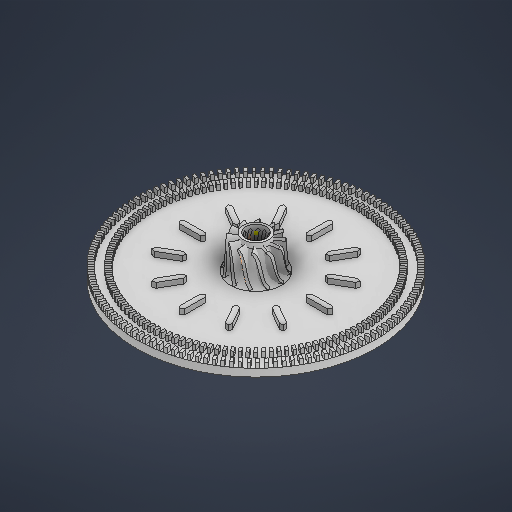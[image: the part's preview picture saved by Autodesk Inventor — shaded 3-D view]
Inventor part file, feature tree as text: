
AUTODESK INVENTOR PART (.ipt)
format: ipt  version: 2025 (Build 290162000, 162)  size: 4,954,624 bytes
history: native  units: mm
features: sketch x10, other x8, extrude x3, pattern_circular x3, revolve x1, projected_geometry x1
ambient origin geometry x8: Origin, YZ Plane, XZ Plane, XY Plane, X Axis, Y Axis, Z Axis, Center Point
bodies: Body1 (feature_tree), Body2 (feature_tree), Body3 (feature_tree)
feature tree (26):
  other  "Твердое тело1"
  revolve  "Вращение1"
  extrude  "Выдавливание1"  Depth=1.5mm
  pattern_circular  "Круговой массив1"  Angle=360.0deg  [1 undecoded]
  other  "РабПлоскость5"
  sketch  "Эскиз8"
  other  "РабПлоскость6"
  sketch  "Эскиз9"
  other  "РабПлоскость7"
  other  "Толщина1"
  pattern_circular  "Круговой массив2"  [2 undecoded]
  sketch  "Эскиз12"
  sketch  "Эскиз13"
  extrude  "Выдавливание2"  Depth=0.5mm
  extrude  "Выдавливание3"  Depth=1.0mm TaperAngle=0.0deg
  pattern_circular  "Круговой массив3"  Count=120 Angle=360.0deg
  sketch  "Эскиз1"
  sketch  "Эскиз2"
  projected_geometry  "Спроецированная петля2"
  sketch  "Эскиз10"
  sketch  "Эскиз11"
  other  "SRF1"
  other  "Твердое тело2"
  sketch  "Эскиз14"
  sketch  "Эскиз15"
  other  "ПврхСеч1"
note: 3 required parameter values undecoded (feature->parameter linkage not recoverable at this tier; creation-order binding heuristic only, values carry confidence <= 0.55)
